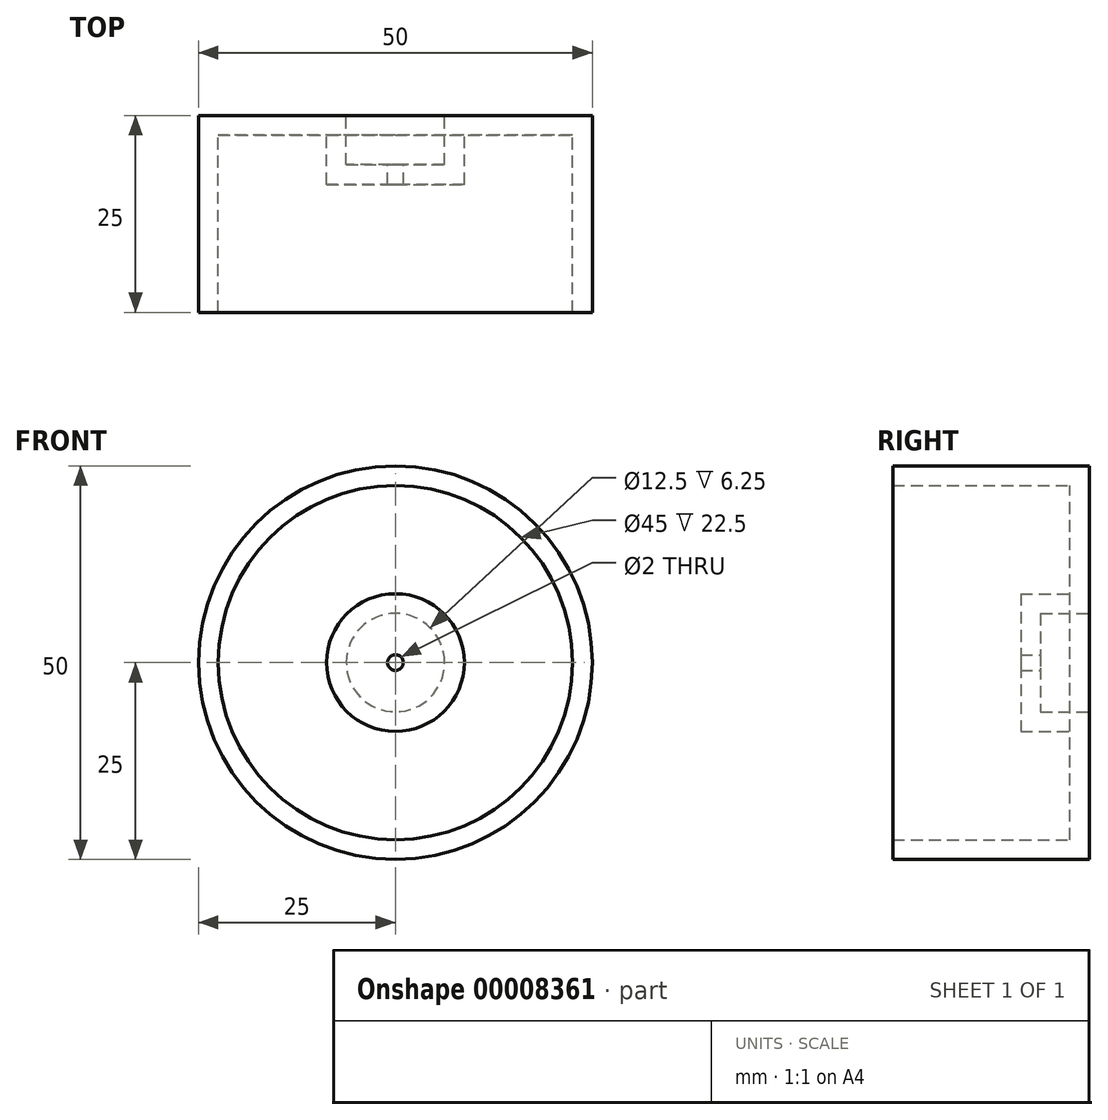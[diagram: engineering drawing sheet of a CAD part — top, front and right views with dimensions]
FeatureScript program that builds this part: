
annotation { "Feature Type Name" : "Feature", "Feature Type Description" : "" }
export const myFeature = defineFeature(function(context is Context, id is Id, definition is map)
    precondition{}
    {
        {
            var Q0;
            Q0=qCreatedBy(makeId("Front.planeOp"),FACE);
            var sketch = newSketch(context, id + "F0", { "sketchPlane" : qUnion([Q0])});
            skCircle(sketch, "E0", {"center": v(0, 0) * mm, "radius": 25 * mm});
            skSolve(sketch);
        }
        {
            var Q0;
            Q0 = qSketchRegion(id + "F0", true);
            extrude(context, id + "F1", {"entities" : qUnion([Q0]), "depth" : 25 * mm});
        }
        {
            var Q0;
            Q0=makeQuery(id+"F1.opExtrude","CAP_FACE",FACE,{"disambiguationData":[OSD([sQuery(id+"F0.wireOp",EDGE,"E0")])],"isStart":true});
            var sketch = newSketch(context, id + "F2", { "sketchPlane" : qUnion([Q0])});
            skCircle(sketch, "E1", {"center": v(0, 0) * mm, "radius": 6.25 * mm});
            skSolve(sketch);
        }
        {
            var Q0;
            Q0=makeQuery(id+"F2.imprint","IMPRINT",FACE,{"disambiguationData":[TD([[makeQuery(id+"F2.imprint","IMPRINT",EDGE,{"derivedFrom":sQuery(id+"F2.wireOp",EDGE,"E1")}),1.0]])]});
            extrude(context, id + "F3", {"entities" : qUnion([Q0]), "operationType" : NewBodyOperationType.REMOVE, "oppositeDirection" : true, "depth" : 6.25 * mm});
        }
        {
            var Q0;
            Q0=makeQuery(id+"F1.opExtrude","CAP_FACE",FACE,{"disambiguationData":[OSD([sQuery(id+"F0.wireOp",EDGE,"E0")])],"isStart":false});
            shell(context, id + "F4", {"entities" : qUnion([Q0]), "thickness" : 2.5 * mm});
        }
        {
            var Q0;
            Q0=makeQuery(id+"F3.boolean.opBoolean","COPY",FACE,{"derivedFrom":makeQuery(id+"F3.opExtrude","CAP_FACE",FACE,{"disambiguationData":[OSD([sQuery(id+"F2.wireOp",EDGE,"E1")])],"isStart":false})});
            var sketch = newSketch(context, id + "F5", { "sketchPlane" : qUnion([Q0])});
            skCircle(sketch, "E2", {"center": v(0, 0) * mm, "radius": 1 * mm});
            skSolve(sketch);
        }
        {
            var Q0;
            Q0 = qSketchRegion(id + "F5", true);
            extrude(context, id + "F6", {"entities" : qUnion([Q0]), "operationType" : NewBodyOperationType.REMOVE, "endBound" : BoundingType.THROUGH_ALL, "oppositeDirection" : true, "depth" : 25 * mm});
        }
    });
